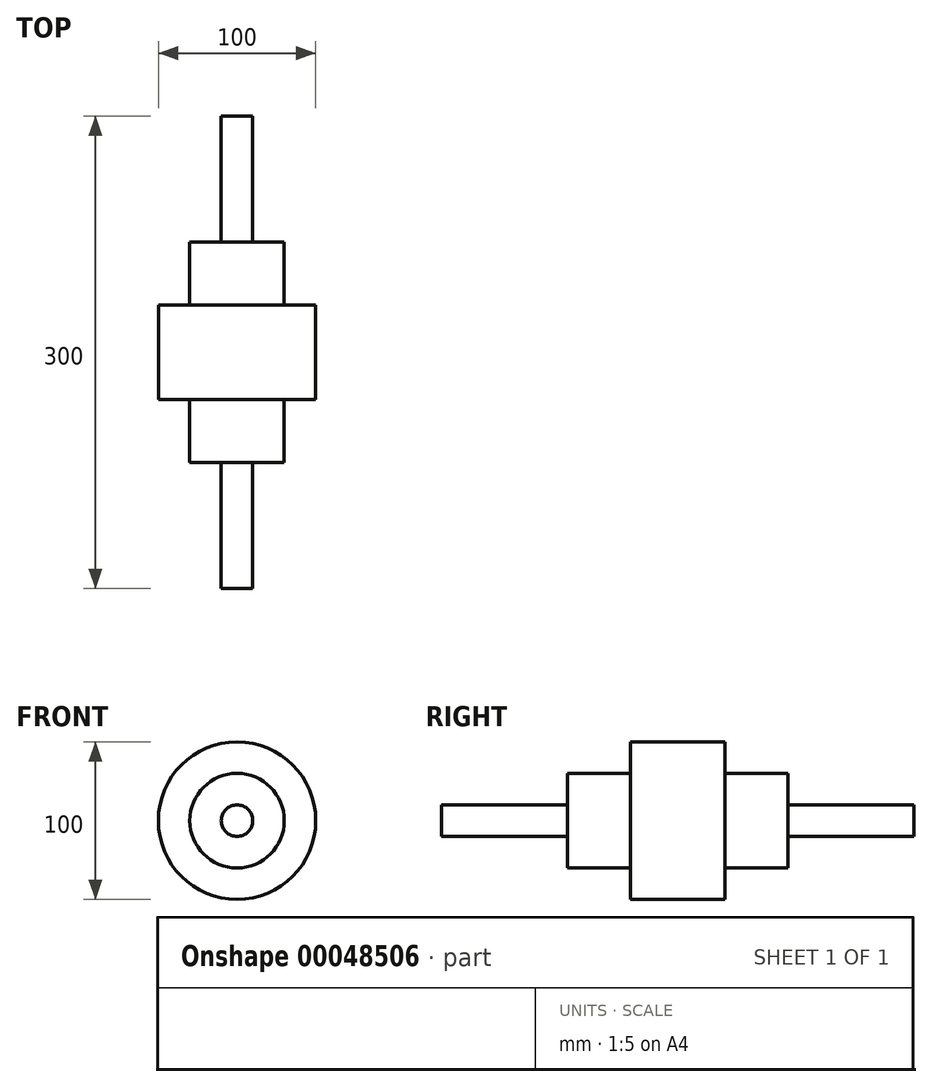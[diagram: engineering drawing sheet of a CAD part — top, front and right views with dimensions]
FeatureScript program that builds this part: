
annotation { "Feature Type Name" : "Feature", "Feature Type Description" : "" }
export const myFeature = defineFeature(function(context is Context, id is Id, definition is map)
    precondition{}
    {
        {
            var Q0;
            Q0=qCreatedBy(makeId("Right.planeOp"),FACE);
            var sketch = newSketch(context, id + "F0", { "sketchPlane" : qUnion([Q0])});
            skLineSegment(sketch, "E0", {"start": v(0, 0) * mm, "end": v(0, 10) * mm});
            skLineSegment(sketch, "E1", {"start": v(0, 10) * mm, "end": v(80, 10) * mm});
            skLineSegment(sketch, "E2", {"start": v(80, 10) * mm, "end": v(80, 30) * mm});
            skLineSegment(sketch, "E3", {"start": v(80, 30) * mm, "end": v(120, 30) * mm});
            skLineSegment(sketch, "E4", {"start": v(120, 30) * mm, "end": v(120, 50) * mm});
            skLineSegment(sketch, "E5", {"start": v(120, 50) * mm, "end": v(180, 50) * mm});
            skLineSegment(sketch, "E6", {"start": v(180, 50) * mm, "end": v(180, 30) * mm});
            skLineSegment(sketch, "E7", {"start": v(180, 30) * mm, "end": v(220, 30) * mm});
            skLineSegment(sketch, "E8", {"start": v(220, 30) * mm, "end": v(220, 10) * mm});
            skLineSegment(sketch, "E9", {"start": v(220, 10) * mm, "end": v(300, 10) * mm});
            skLineSegment(sketch, "E10", {"start": v(300, 10) * mm, "end": v(300, 0) * mm});
            skLineSegment(sketch, "E11", {"start": v(300, 0) * mm, "end": v(0, 0) * mm});
            skSolve(sketch);
        }
        {
            var Q0;
            Q0=makeQuery(id+"F0.imprint","IMPRINT",FACE,{"disambiguationData":[TD([[makeQuery(id+"F0.imprint","IMPRINT",EDGE,{"derivedFrom":sQuery(id+"F0.wireOp",EDGE,"E0")}),-1.0]])]});
            var Q1;
            Q1=sQuery(id+"F0.wireOp",EDGE,"E11");
            revolve(context, id + "F1", {"entities" : qUnion([Q0]), "axis" : qUnion([Q1]), "revolveType" : RevolveType.FULL});
        }
    });
